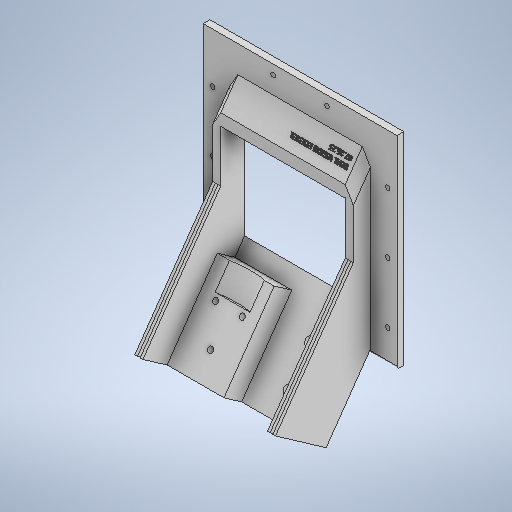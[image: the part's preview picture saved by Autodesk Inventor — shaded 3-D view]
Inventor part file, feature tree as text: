
AUTODESK INVENTOR PART (.ipt)
format: ipt  version: 2025.2 (Build 292293000, 293)  size: 1,317,888 bytes
history: native  units: in
note: dims shown in document units (in); Inventor stores cm internally (conversion verified against a paired STEP export)
features: sketch x35, extrude x30, plane x5, projected_geometry x3, move_body x1, chamfer x1, fillet x1, hole x1
ambient origin geometry x8: Origin, YZ Plane, XZ Plane, XY Plane, X Axis, Y Axis, Z Axis, Center Point
bodies: Solid1 (feature_tree)
feature tree (77):
  extrude  "Extrusion1"  Depth=0.1969in TaperAngle=0.0deg
  move_body  "Move Body1"
  plane  "Work Plane1"
  sketch  "Sketch5"  dims[d5=1.7717in d6=1.7717in d7=1.7717in d8=1.7717in d9=0.8108in d10=90.0deg d11=0.0787in d12=0.3701in d13=0.4252in d14=0.1362in d15=-0.0984in d16=-0.0591in d17=0.0in]
  plane  "Work Plane2"
  extrude  "Extrusion4"  TaperAngle=0.0deg  [1 undecoded]
  extrude  "Extrusion6"  Depth=0.2405in
  extrude  "Extrusion8"  Depth=2.5591in TaperAngle=0.0deg
  chamfer  "Chamfer1"  [1 undecoded]
  extrude  "Extrusion11"  Depth=0.2362in
  plane  "Work Plane3"
  extrude  "Extrusion13"  Depth=0.1969in TaperAngle=0.0deg
  plane  "Work Plane4"
  plane  "Work Plane6"
  extrude  "Extrusion21"  Depth=0.5027in
  extrude  "Extrusion22"  Depth=0.5027in
  extrude  "Extrusion25"  Depth=1.1811in TaperAngle=0.0deg
  extrude  "Extrusion26"  Depth=0.1969in
  sketch  "Sketch33"  dims[d100=3.6403in d101=2.7717in]
  extrude  "Extrusion27"  Depth=0.2362in TaperAngle=0.0deg
  extrude  "Extrusion28"  Depth=3.6403in
  sketch  "Sketch36"  dims[d124=0.9712in d125=0.0in d126=0.5906in d127=0.0in]
  extrude  "Extrusion29"  Depth=0.6299in TaperAngle=0.0deg
  extrude  "Extrusion30"  Depth=0.1575in
  extrude  "Extrusion31"  Depth=0.5906in TaperAngle=0.0deg
  sketch  "Sketch39"  dims[d139=0.1181in d140=0.0in d141=0.6299in]
  extrude  "Extrusion32"  Depth=11.3469in TaperAngle=0.0deg
  fillet  "Fillet1"  Radius=0.4331in
  extrude  "Extrusion33"  Depth=0.4331in
  extrude  "Extrusion34"  Depth=0.1181in
  extrude  "Extrusion35"  Depth=0.0787in
  sketch  "Sketch45"  dims[d164=0.1181in d165=0.0in d168=0.5906in d169=0.0in]
  extrude  "Extrusion37"  TaperAngle=0.0deg  [1 undecoded]
  extrude  "Extrusion38"  Depth=0.1181in TaperAngle=0.0deg
  extrude  "Extrusion40"  Depth=0.1181in TaperAngle=0.0deg
  extrude  "Extrusion41"  Depth=0.1181in TaperAngle=0.0deg
  extrude  "Extrusion43"  TaperAngle=0.0deg  [1 undecoded]
  extrude  "Extrusion44"  TaperAngle=0.0deg  [1 undecoded]
  extrude  "Extrusion46"  TaperAngle=0.0deg  [1 undecoded]
  extrude  "Extrusion47"  Depth=0.5906in
  extrude  "Extrusion48"  Depth=0.0394in TaperAngle=0.0deg
  sketch  "Sketch61"  dims[d58=0.0344in]
  extrude  "Extrusion50"  Depth=3.9671in TaperAngle=0.0deg
  extrude  "Extrusion51"  Depth=0.0197in
  sketch  "Sketch1"  dims[d1=0.5512in d2=0.1969in d3=0.0in]
  sketch  "Sketch6"  dims[d18=0.2749in d24=0.2405in]
  sketch  "Sketch8"  dims[d25=2.7559in d26=0.0in d29=2.5591in d30=0.0in d36=0.0in d37=0.0in]
  sketch  "Sketch12"  dims[d42=0.2362in d43=0.2362in]
  sketch  "Sketch15"  dims[d52=0.2362in d53=0.0787in d54=45.0deg d55=0.1969in d56=0.0in]
  sketch  "Sketch17"  dims[d59=0.5906in d60=0.0in d76=0.5027in]
  sketch  "Sketch27"  dims[d77=0.5027in d78=0.5027in]
  sketch  "Sketch28"  dims[d79=0.5027in d81=1.1811in d82=0.0in]
  sketch  "Sketch31"  dims[d83=0.0in d84=0.0in d91=0.1969in]
  sketch  "Sketch32"  dims[d94=0.2362in d95=0.0in d96=0.2362in d97=0.0in]
  sketch  "Sketch34"  dims[d112=1.9685in d113=0.6299in d114=0.0in]
  sketch  "Sketch35"  dims[d115=0.1575in d117=0.1575in d121=1.9685in d122=0.7874in d123=0.9331in]
  sketch  "Sketch37"  dims[d128=11.3469in d129=0.0in d130=11.3469in d131=0.0in d136=0.4331in]
  sketch  "Sketch38"  dims[d137=0.4331in d138=0.4331in]
  sketch  "Sketch40"  dims[d142=0.0787in d147=0.2756in]
  sketch  "Sketch41"  dims[d149=0.2756in d150=0.0in d151=0.0in]
  sketch  "Sketch42"  dims[d154=0.1181in d155=0.0in d156=0.1181in d157=0.0in]
  sketch  "Sketch44"  dims[d158=0.5906in d160=0.1181in d161=0.0in d162=0.1969in d163=0.0in]
  projected_geometry  "Projected Loop2"
  projected_geometry  "Projected Loop3"
  projected_geometry  "Projected Loop5"
  sketch  "Sketch47"  dims[d170=4.7244in d171=0.0in d174=0.0in d175=0.0in]
  sketch  "Sketch49"  dims[d176=0.7313in d177=0.0in d186=0.0in d187=0.0in]
  sketch  "Sketch50"  dims[d188=0.0in d189=0.0in d194=0.0in d195=0.0in]
  sketch  "Sketch52"  dims[d196=1.1024in d197=0.5906in]
  sketch  "Sketch53"  dims[d198=0.0394in d199=0.0in d200=0.0394in d201=0.0in]
  sketch  "Sketch56"  dims[d235=6.1063in d236=0.0in d244=3.9671in d245=0.0in]
  sketch  "Sketch58"  dims[d246=0.9963in d38=0.0197in]
  sketch  "Sketch59"  dims[d39=0.0344in d57=0.0197in]
  sketch  "Sketch63"  dims[d159=0.0344in]
  sketch  "Sketch64"  dims[d178=0.0in d179=0.0in d180=0.0in d181=0.0in d202=0.0197in d203=0.0344in]
  sketch  "Sketch2"  dims[d4=0.315in]
  hole  "Hole1"  [1 undecoded]
note: 7 required parameter values undecoded (feature->parameter linkage not recoverable at this tier; creation-order binding heuristic only, values carry confidence <= 0.55)
